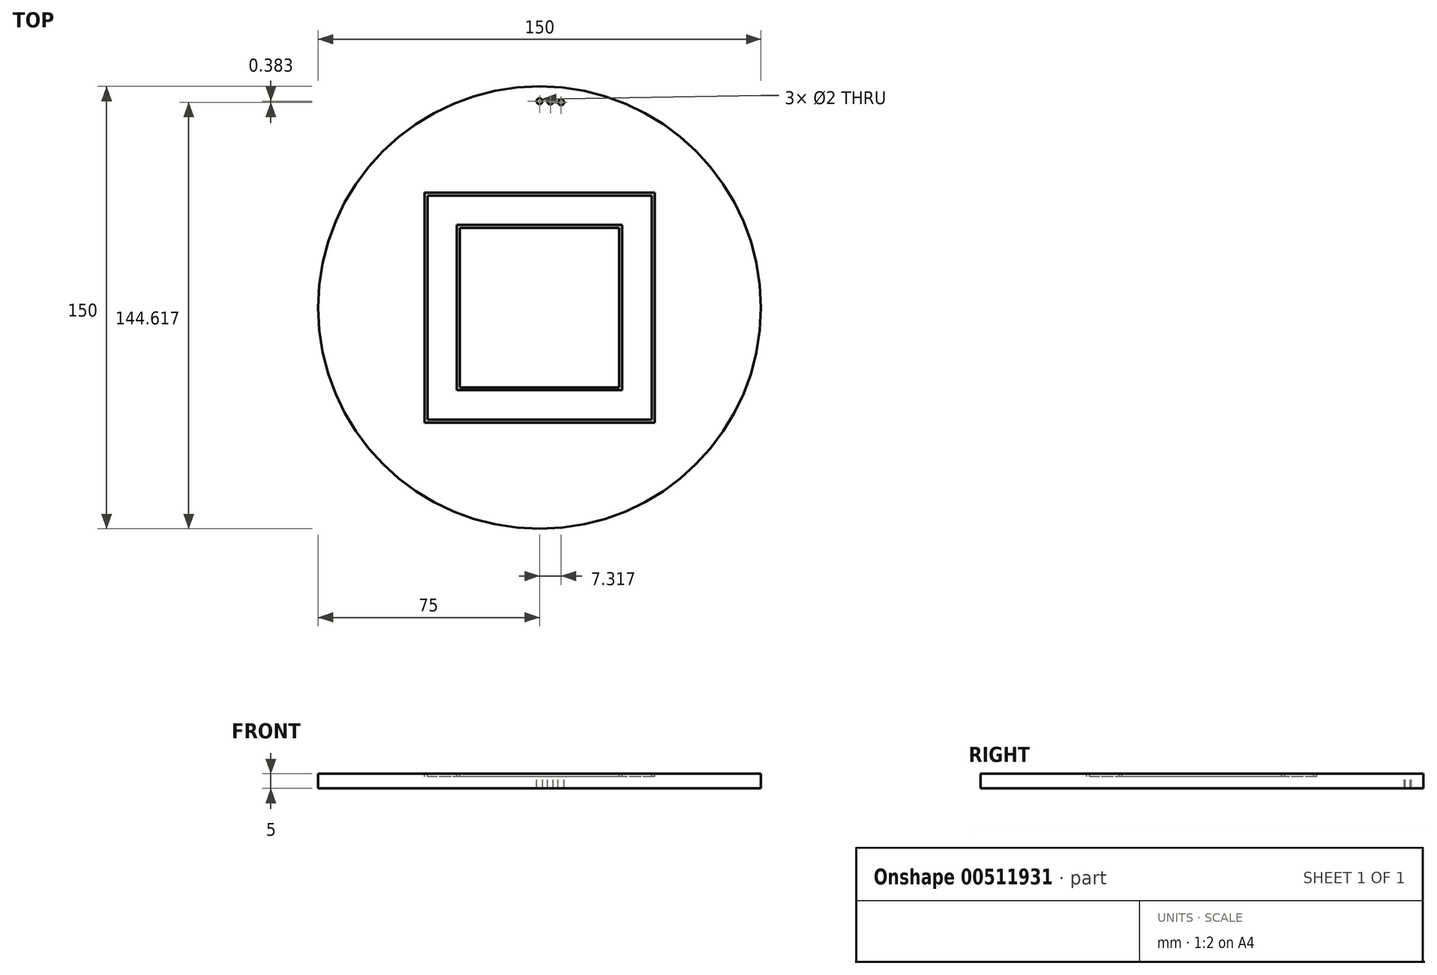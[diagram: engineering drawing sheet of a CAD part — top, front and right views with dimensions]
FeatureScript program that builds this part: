
annotation { "Feature Type Name" : "Feature", "Feature Type Description" : "" }
export const myFeature = defineFeature(function(context is Context, id is Id, definition is map)
    precondition{}
    {
        {
            var Q0;
            Q0=qCreatedBy(makeId("Top.planeOp"),FACE);
            var sketch = newSketch(context, id + "F0", { "sketchPlane" : qUnion([Q0])});
            skCircle(sketch, "E0", {"center": v(0, 0) * mm, "radius": 75 * mm});
            skSolve(sketch);
        }
        {
            var Q0;
            Q0 = qSketchRegion(id + "F0", true);
            extrude(context, id + "F1", {"entities" : qUnion([Q0]), "depth" : 5 * mm});
        }
        {
            var Q0;
            Q0=makeQuery(id+"F1.opExtrude","CAP_FACE",FACE,{"disambiguationData":[OSD([sQuery(id+"F0.wireOp",EDGE,"E0")])],"isStart":false});
            var sketch = newSketch(context, id + "F2", { "sketchPlane" : qUnion([Q0])});
            skLineSegment(sketch, "E1.bottom", {"start": v(27, 27) * mm, "end": v(-27, 27) * mm});
            skLineSegment(sketch, "E1.top", {"start": v(27, -27) * mm, "end": v(-27, -27) * mm});
            skLineSegment(sketch, "E1.left", {"start": v(27, 27) * mm, "end": v(27, -27) * mm});
            skLineSegment(sketch, "E1.right", {"start": v(-27, 27) * mm, "end": v(-27, -27) * mm});
            skPoint(sketch, "E1.middle", {"position": v(0, 0) * mm});
            skLineSegment(sketch, "E2.bottom", {"start": v(38, 38) * mm, "end": v(-38, 38) * mm});
            skLineSegment(sketch, "E2.top", {"start": v(38, -38) * mm, "end": v(-38, -38) * mm});
            skLineSegment(sketch, "E2.left", {"start": v(38, 38) * mm, "end": v(38, -38) * mm});
            skLineSegment(sketch, "E2.right", {"start": v(-38, 38) * mm, "end": v(-38, -38) * mm});
            skLineSegment(sketch, "E3.0", {"start": v(39, 39) * mm, "end": v(39, -39) * mm});
            skLineSegment(sketch, "E3.1", {"start": v(39, 39) * mm, "end": v(-39, 39) * mm});
            skLineSegment(sketch, "E3.2", {"start": v(-39, 39) * mm, "end": v(-39, -39) * mm});
            skLineSegment(sketch, "E3.3", {"start": v(39, -39) * mm, "end": v(-39, -39) * mm});
            skLineSegment(sketch, "E4.0", {"start": v(28, 28) * mm, "end": v(28, -28) * mm});
            skLineSegment(sketch, "E4.1", {"start": v(28, 28) * mm, "end": v(-28, 28) * mm});
            skLineSegment(sketch, "E4.2", {"start": v(-28, 28) * mm, "end": v(-28, -28) * mm});
            skLineSegment(sketch, "E4.3", {"start": v(28, -28) * mm, "end": v(-28, -28) * mm});
            skSolve(sketch);
        }
        {
            var Q0;
            Q0 = qSketchRegion(id + "F2", true);
            var Q1;
            Q1=makeQuery(id+"F2.imprint","IMPRINT",FACE,{"disambiguationData":[TD([[makeQuery(id+"F2.imprint","IMPRINT",EDGE,{"derivedFrom":sQuery(id+"F2.wireOp",EDGE,"E1.bottom")}),-1.0]])]});
            extrude(context, id + "F3", {"entities" : qUnion([Q0, Q1]), "operationType" : NewBodyOperationType.REMOVE, "oppositeDirection" : true, "depth" : 1 * mm});
        }
        {
            var Q0;
            {var subQ0=sQuery(id+"F0.wireOp",EDGE,"E0");Q0=makeQuery(id+"F3.boolean.opBoolean","SPLIT",FACE,{"disambiguationData":[TD([makeQuery(id+"F1.opExtrude","SWEPT_FACE",FACE,{"disambiguationData":[OSD([subQ0])]})])],"derivedFrom":makeQuery(id+"F1.opExtrude","CAP_FACE",FACE,{"disambiguationData":[OSD([subQ0])],"isStart":false})});}
            var sketch = newSketch(context, id + "F4", { "sketchPlane" : qUnion([Q0])});
            skCircle(sketch, "E5", {"center": v(0, 0) * mm, "radius": 70 * mm, "construction": true});
            skCircle(sketch, "E6", {"center": v(0, 70) * mm, "radius": 1 * mm});
            skCircle(sketch, "E7", {"center": v(3.66, 69.9) * mm, "radius": 1 * mm});
            skCircle(sketch, "E8", {"center": v(7.32, 69.62) * mm, "radius": 1 * mm});
            skLineSegment(sketch, "E9", {"start": v(3.66, 69.9) * mm, "end": v(0, 0) * mm, "construction": true});
            skLineSegment(sketch, "E10", {"start": v(0, 70) * mm, "end": v(0, 0) * mm, "construction": true});
            skLineSegment(sketch, "E11", {"start": v(7.32, 69.62) * mm, "end": v(0, 0) * mm, "construction": true});
            skSolve(sketch);
        }
        {
            var Q0;
            Q0 = qSketchRegion(id + "F4", true);
            extrude(context, id + "F5", {"entities" : qUnion([Q0]), "operationType" : NewBodyOperationType.REMOVE, "endBound" : BoundingType.THROUGH_ALL, "oppositeDirection" : true, "depth" : 25 * mm});
        }
    });
